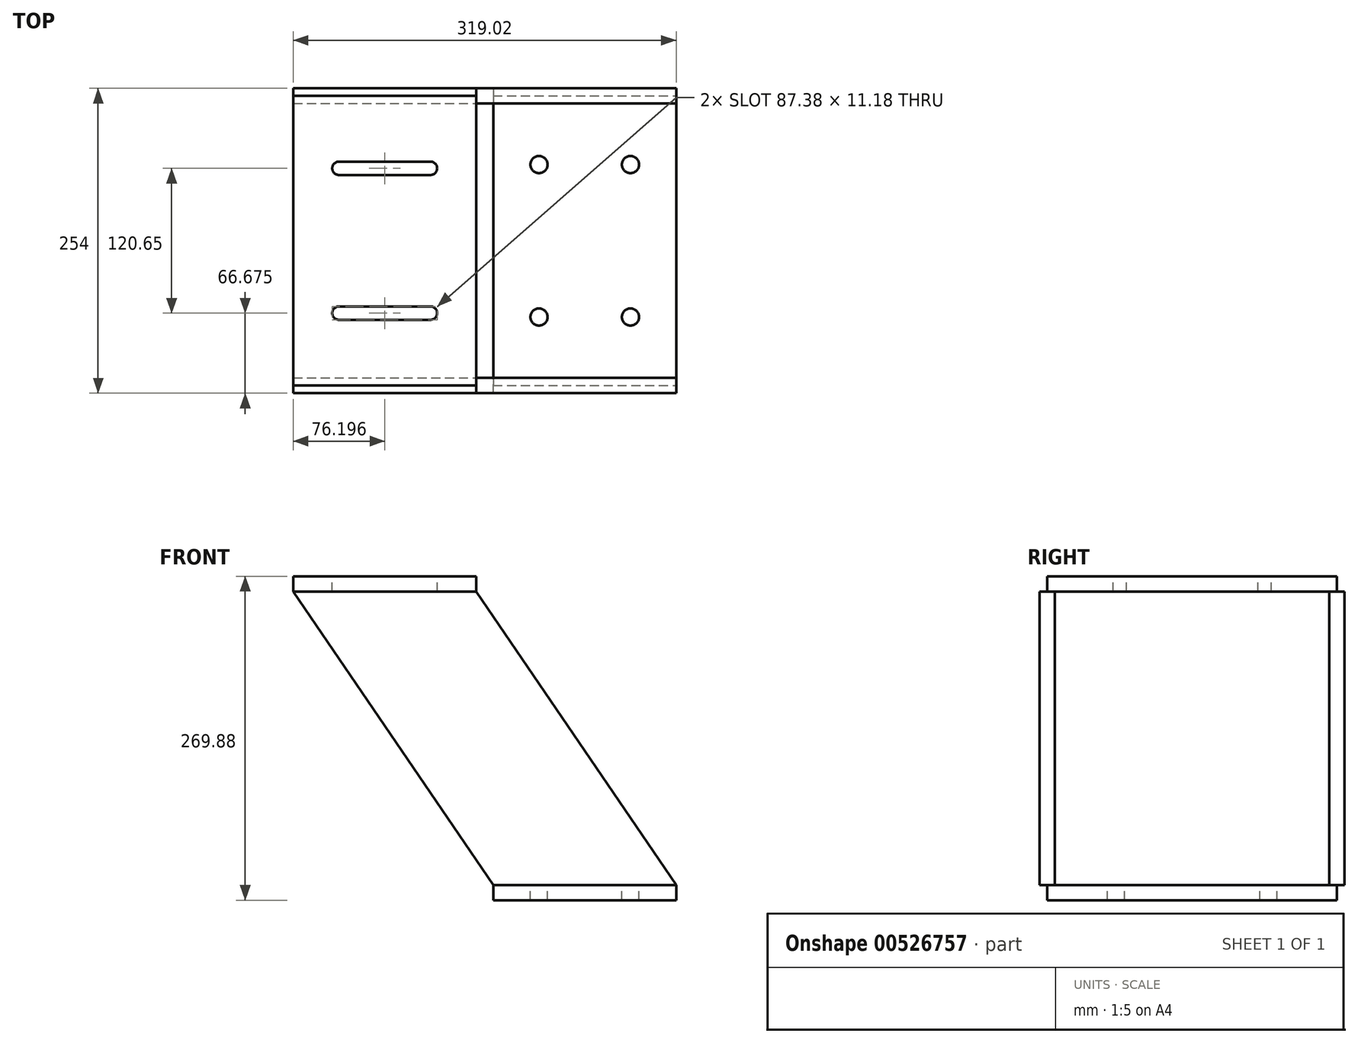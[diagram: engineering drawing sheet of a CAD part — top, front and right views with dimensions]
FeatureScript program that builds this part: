
annotation { "Feature Type Name" : "Feature", "Feature Type Description" : "" }
export const myFeature = defineFeature(function(context is Context, id is Id, definition is map)
    precondition{}
    {
        {
            var Q0;
            Q0=qCreatedBy(makeId("Top.planeOp"),FACE);
            var sketch = newSketch(context, id + "F0", { "sketchPlane" : qUnion([Q0])});
            skLineSegment(sketch, "E0.bottom", {"start": v(-76.2, 120.65) * mm, "end": v(76.2, 120.65) * mm});
            skLineSegment(sketch, "E0.top", {"start": v(-76.2, -120.65) * mm, "end": v(76.2, -120.65) * mm});
            skLineSegment(sketch, "E0.left", {"start": v(-76.2, 120.65) * mm, "end": v(-76.2, -120.65) * mm});
            skLineSegment(sketch, "E0.right", {"start": v(76.2, 120.65) * mm, "end": v(76.2, -120.65) * mm});
            skPoint(sketch, "E0.middle", {"position": v(0, 0) * mm});
            skSolve(sketch);
        }
        {
            var Q0;
            Q0 = qSketchRegion(id + "F0", true);
            extrude(context, id + "F1", {"entities" : qUnion([Q0]), "depth" : 12.7 * mm, "offsetDistance" : 25.4 * mm});
        }
        {
            var Q0;
            Q0=makeQuery(id+"F1.opExtrude","CAP_FACE",FACE,{"disambiguationData":[OSD([sQuery(id+"F0.wireOp",EDGE,"E0.bottom"),sQuery(id+"F0.wireOp",EDGE,"E0.top"),sQuery(id+"F0.wireOp",EDGE,"E0.left"),sQuery(id+"F0.wireOp",EDGE,"E0.right")])],"isStart":false});
            var sketch = newSketch(context, id + "F2", { "sketchPlane" : qUnion([Q0])});
            skLineSegment(sketch, "E1", {"start": v(0, 141.74) * mm, "end": v(0, -149.96) * mm, "construction": true});
            skPoint(sketch, "E1.endSnap0", {"position": v(0, -120.65) * mm});
            skLineSegment(sketch, "E2", {"start": v(-146.2, 0) * mm, "end": v(146.2, 0) * mm, "construction": true});
            skLineSegment(sketch, "E3.0", {"start": v(-38.1, 141.74) * mm, "end": v(-38.1, -149.96) * mm, "construction": true});
            skLineSegment(sketch, "E4.0", {"start": v(-146.2, -63.5) * mm, "end": v(146.2, -63.5) * mm, "construction": true});
            skPoint(sketch, "E5", {"position": v(-38.1, -63.5) * mm});
            skPoint(sketch, "E6.0.1.0", {"position": v(-38.1, 63.5) * mm});
            skPoint(sketch, "E6.1.0.0", {"position": v(38.1, -63.5) * mm});
            skPoint(sketch, "E6.1.1.0", {"position": v(38.1, 63.5) * mm});
            skLineSegment(sketch, "E6.direction1", {"start": v(-38.1, -63.5) * mm, "end": v(38.1, -63.5) * mm, "construction": true});
            skLineSegment(sketch, "E6.direction2", {"start": v(-38.1, -63.5) * mm, "end": v(-38.1, 63.5) * mm, "construction": true});
            skSolve(sketch);
        }
        {
            var Q0;
            Q0=sQuery(id+"F2.wireOp",VERTEX,"E6.0.1.0");
            var Q1;
            Q1=sQuery(id+"F2.wireOp",VERTEX,"E6.1.1.0");
            var Q2;
            Q2=sQuery(id+"F2.wireOp",VERTEX,"E5");
            var Q3;
            Q3=sQuery(id+"F2.wireOp",VERTEX,"E6.1.0.0");
            var Q4;
            Q4=makeQuery(id+"F1.opExtrude","SWEPT_BODY",BODY,{"disambiguationData":[OSD([sQuery(id+"F0.wireOp",EDGE,"E0.bottom"),sQuery(id+"F0.wireOp",EDGE,"E0.top"),sQuery(id+"F0.wireOp",EDGE,"E0.left"),sQuery(id+"F0.wireOp",EDGE,"E0.right")])]});
            hole(context, id + "F3", {"style" : HoleStyle.SIMPLE, "endStyle" : HoleEndStyle.THROUGH, "holeDiameter" : 14.29 * mm, "isTappedThrough" : true, "tappedDepth" : 24.82 * mm, "tapClearance" : 3, "locations" : qUnion([Q0, Q1, Q2, Q3]), "scope" : qUnion([Q4])});
        }
        {
            var Q0;
            Q0=makeQuery(id+"F1.opExtrude","CAP_FACE",FACE,{"disambiguationData":[OSD([sQuery(id+"F0.wireOp",EDGE,"E0.bottom"),sQuery(id+"F0.wireOp",EDGE,"E0.top"),sQuery(id+"F0.wireOp",EDGE,"E0.left"),sQuery(id+"F0.wireOp",EDGE,"E0.right")])],"isStart":true});
            cPlane(context, id + "F4", {"entities" : qUnion([Q0]), "cplaneType" : CPlaneType.OFFSET, "offset" : 269.88 * mm, "oppositeDirection" : true, "width" : 152.4 * mm, "height" : 152.4 * mm});
        }
        {
            var Q0;
            Q0=qCreatedBy(id+"F4.planeOp",FACE);
            var sketch = newSketch(context, id + "F5", { "sketchPlane" : qUnion([Q0])});
            skLineSegment(sketch, "E7", {"start": v(0, -137.74) * mm, "end": v(0, 137.74) * mm, "construction": true});
            skLineSegment(sketch, "E8", {"start": v(142.36, 0) * mm, "end": v(-232.65, 0) * mm, "construction": true});
            skLineSegment(sketch, "E9.0", {"start": v(-166.62, -137.74) * mm, "end": v(-166.62, 0) * mm, "construction": true});
            skLineSegment(sketch, "E10.bottom", {"start": v(-242.82, -120.65) * mm, "end": v(-90.42, -120.65) * mm});
            skLineSegment(sketch, "E10.top", {"start": v(-242.82, 120.65) * mm, "end": v(-90.42, 120.65) * mm});
            skLineSegment(sketch, "E10.left", {"start": v(-242.82, -120.65) * mm, "end": v(-242.82, 120.65) * mm});
            skLineSegment(sketch, "E10.right", {"start": v(-90.42, -120.65) * mm, "end": v(-90.42, 120.65) * mm});
            skPoint(sketch, "E10.middle", {"position": v(-166.62, 0) * mm});
            skSolve(sketch);
        }
        {
            var Q0;
            Q0 = qSketchRegion(id + "F5", true);
            extrude(context, id + "F6", {"entities" : qUnion([Q0]), "depth" : 12.7 * mm, "offsetDistance" : 25.4 * mm});
        }
        {
            var Q0;
            Q0=makeQuery(id+"F6.opExtrude","CAP_FACE",FACE,{"disambiguationData":[OSD([sQuery(id+"F5.wireOp",EDGE,"E10.bottom"),sQuery(id+"F5.wireOp",EDGE,"E10.top"),sQuery(id+"F5.wireOp",EDGE,"E10.left"),sQuery(id+"F5.wireOp",EDGE,"E10.right")])],"isStart":true});
            var sketch = newSketch(context, id + "F7", { "sketchPlane" : qUnion([Q0])});
            skLineSegment(sketch, "E11", {"start": v(143.39, 0) * mm, "end": v(-362.6, 0) * mm, "construction": true});
            skLineSegment(sketch, "E12", {"start": v(-166.62, 120.65) * mm, "end": v(-166.62, -120.65) * mm, "construction": true});
            skLineSegment(sketch, "E13.0", {"start": v(-204.72, 120.65) * mm, "end": v(-204.72, -120.65) * mm, "construction": true});
            skLineSegment(sketch, "E14", {"start": v(-204.72, 60.32) * mm, "end": v(-128.52, 60.32) * mm});
            skArc(sketch, "E15.0.startCap", {"start": v(-204.72, 54.74) * mm, "mid": v(-210.31, 60.32) * mm, "end": v(-204.72, 65.91) * mm});
            skArc(sketch, "E15.0.endCap", {"start": v(-128.52, 65.91) * mm, "mid": v(-122.94, 60.32) * mm, "end": v(-128.52, 54.74) * mm});
            skLineSegment(sketch, "E15.0.left", {"start": v(-204.72, 65.91) * mm, "end": v(-128.52, 65.91) * mm});
            skLineSegment(sketch, "E15.0.right", {"start": v(-204.72, 54.74) * mm, "end": v(-128.52, 54.74) * mm});
            skArc(sketch, "E16.MirrorCS", {"start": v(-204.72, -54.74) * mm, "mid": v(-210.31, -60.32) * mm, "end": v(-204.72, -65.91) * mm});
            skLineSegment(sketch, "E17.MirrorCS", {"start": v(-204.72, -60.32) * mm, "end": v(-128.52, -60.32) * mm});
            skArc(sketch, "E18.MirrorCS", {"start": v(-128.52, -65.91) * mm, "mid": v(-122.94, -60.32) * mm, "end": v(-128.52, -54.74) * mm});
            skLineSegment(sketch, "E19.MirrorCS", {"start": v(-204.72, -65.91) * mm, "end": v(-128.52, -65.91) * mm});
            skLineSegment(sketch, "E20.MirrorCS", {"start": v(-204.72, -54.74) * mm, "end": v(-128.52, -54.74) * mm});
            skSolve(sketch);
        }
        {
            var Q0;
            Q0 = qSketchRegion(id + "F7", true);
            extrude(context, id + "F8", {"entities" : qUnion([Q0]), "operationType" : NewBodyOperationType.REMOVE, "endBound" : BoundingType.THROUGH_ALL, "oppositeDirection" : true, "depth" : 25.4 * mm, "offsetDistance" : 25.4 * mm});
        }
        {
            var Q0;
            Q0=makeQuery(id+"F1.opExtrude","SWEPT_FACE",FACE,{"disambiguationData":[OSD([sQuery(id+"F0.wireOp",EDGE,"E0.top")])]});
            var sketch = newSketch(context, id + "F9", { "sketchPlane" : qUnion([Q0])});
            skLineSegment(sketch, "E21.0", {"start": v(-242.82, 257.18) * mm, "end": v(-90.42, 257.18) * mm});
            skLineSegment(sketch, "E22.0", {"start": v(-76.2, 12.7) * mm, "end": v(76.2, 12.7) * mm});
            skLineSegment(sketch, "E23", {"start": v(-242.82, 257.18) * mm, "end": v(-76.2, 12.7) * mm});
            skLineSegment(sketch, "E24", {"start": v(-90.42, 257.18) * mm, "end": v(76.2, 12.7) * mm});
            skSolve(sketch);
        }
        {
            var Q0;
            Q0 = qSketchRegion(id + "F9", true);
            extrude(context, id + "F10", {"entities" : qUnion([Q0]), "endBound" : BoundingType.SYMMETRIC, "depth" : 12.7 * mm, "offsetDistance" : 25.4 * mm});
        }
        {
            var Q0;
            Q0=makeQuery(id+"F10.opExtrude","SWEPT_BODY",BODY,{"disambiguationData":[OSD([sQuery(id+"F9.wireOp",EDGE,"E21.0"),sQuery(id+"F9.wireOp",EDGE,"E22.0"),sQuery(id+"F9.wireOp",EDGE,"E23"),sQuery(id+"F9.wireOp",EDGE,"E24")])]});
            var Q1;
            Q1=qCreatedBy(makeId("Front.planeOp"),FACE);
            mirror(context, id + "F11", {"entities" : qUnion([Q0]), "mirrorPlane" : qUnion([Q1])});
        }
    });
